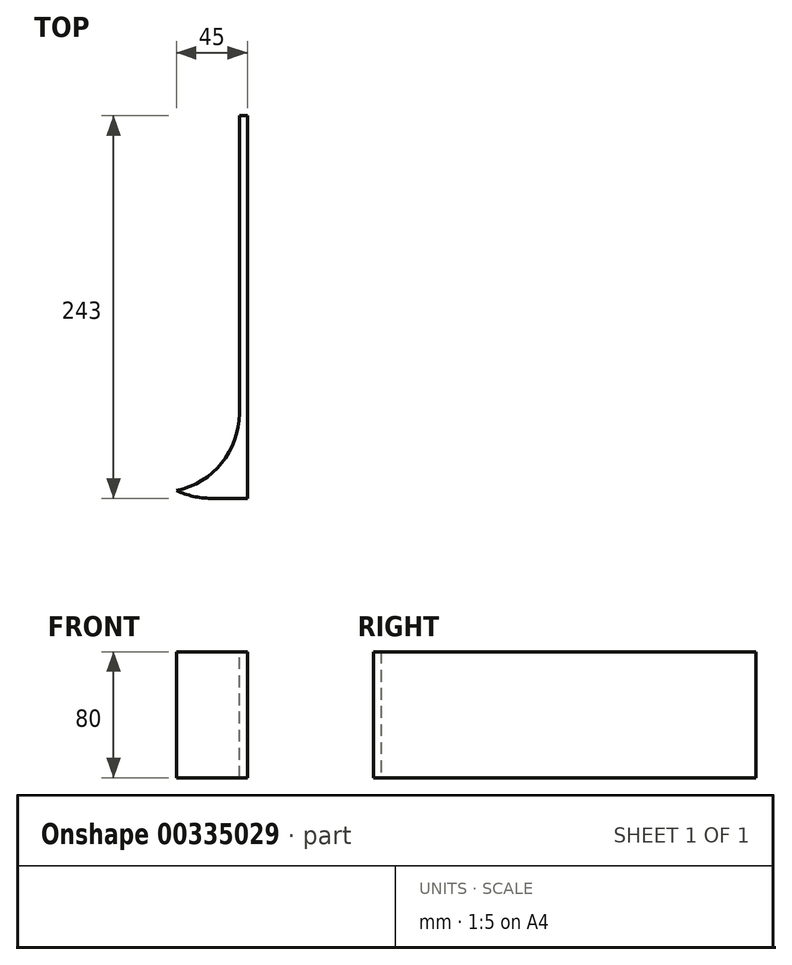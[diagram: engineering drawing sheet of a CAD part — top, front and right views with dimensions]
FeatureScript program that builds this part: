
annotation { "Feature Type Name" : "Feature", "Feature Type Description" : "" }
export const myFeature = defineFeature(function(context is Context, id is Id, definition is map)
    precondition{}
    {
        {
            var Q0;
            Q0=qCreatedBy(makeId("Top.planeOp"),FACE);
            var sketch = newSketch(context, id + "F0", { "sketchPlane" : qUnion([Q0])});
            skLineSegment(sketch, "E0.bottom", {"start": v(2.5, -121.5) * mm, "end": v(-2.5, -121.5) * mm});
            skLineSegment(sketch, "E0.top", {"start": v(2.5, 121.5) * mm, "end": v(-2.5, 121.5) * mm});
            skLineSegment(sketch, "E0.left", {"start": v(2.5, -121.5) * mm, "end": v(2.5, 121.5) * mm});
            skLineSegment(sketch, "E0.right", {"start": v(-2.5, -121.5) * mm, "end": v(-2.5, 121.5) * mm});
            skPoint(sketch, "E0.middle", {"position": v(0, 0) * mm});
            skLineSegment(sketch, "E1.bottom", {"start": v(2.5, -121.5) * mm, "end": v(-42.5, -121.5) * mm});
            skLineSegment(sketch, "E1.top", {"start": v(2.5, -116.5) * mm, "end": v(-42.5, -116.5) * mm});
            skLineSegment(sketch, "E1.left", {"start": v(2.5, -121.5) * mm, "end": v(2.5, -116.5) * mm});
            skLineSegment(sketch, "E1.right", {"start": v(-42.5, -121.5) * mm, "end": v(-42.5, -116.5) * mm});
            skSolve(sketch);
        }
        {
            var Q0;
            Q0=qSketchRegion(id+"F0",true);
            extrude(context, id + "F1", {"entities" : qUnion([Q0]), "depth" : 80 * mm});
        }
        {
            var Q0;
            Q0=makeQuery(id+"F1.opExtrude","SWEPT_EDGE",EDGE,{"disambiguationData":[OSD([sQuery(id+"F0.wireOp",EDGE,"E1.bottom"),sQuery(id+"F0.wireOp",EDGE,"E1.left")])]});
            var Q1;
            Q1=makeQuery(id+"F1.opExtrude","SWEPT_EDGE",EDGE,{"disambiguationData":[OSD([sQuery(id+"F0.wireOp",EDGE,"E0.right"),sQuery(id+"F0.wireOp",EDGE,"E1.top")])]});
            fillet(context, id + "F2", {"entities" : qUnion([Q0, Q1]), "radius" : 50 * mm, "tangentPropagation" : true, "allowEdgeOverflow" : false});
        }
    });
